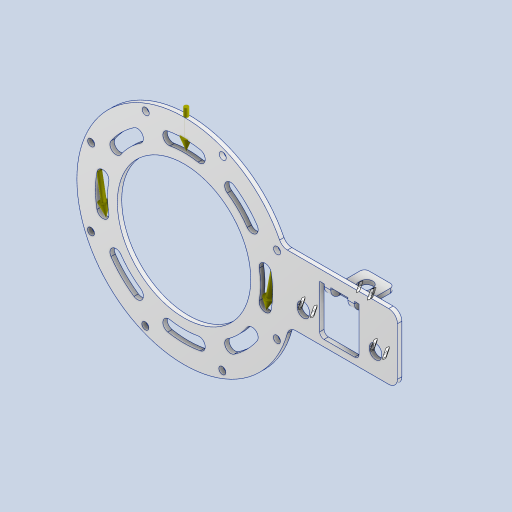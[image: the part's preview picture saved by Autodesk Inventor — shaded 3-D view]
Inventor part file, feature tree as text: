
AUTODESK INVENTOR PART (.ipt)
format: ipt  version: 2023 (Build 270158000, 158)  size: 1,698,816 bytes
history: native  units: mm
features: other x5, fillet x2, extrude x1, sketch x1
ambient origin geometry x8: Origin, YZ Plane, XZ Plane, XY Plane, X Axis, Y Axis, Z Axis, Center Point
bodies: Body1 (feature_tree), Body2 (feature_tree)
feature tree (9):
  other  "GIM8108-8_1.ipt"
  extrude  "押し出し2"  Depth=10.0mm
  fillet  "フィレット4"  Radius=98.0mm
  other  "折り曲げ3"
  fillet  "フィレット5"  Radius=3.2mm
  other  "TaggingFeature1"
  sketch  "スケッチ17"
  other  "ソリッド1::GIM8108-8_1.ipt"
  other  "Srf1"
